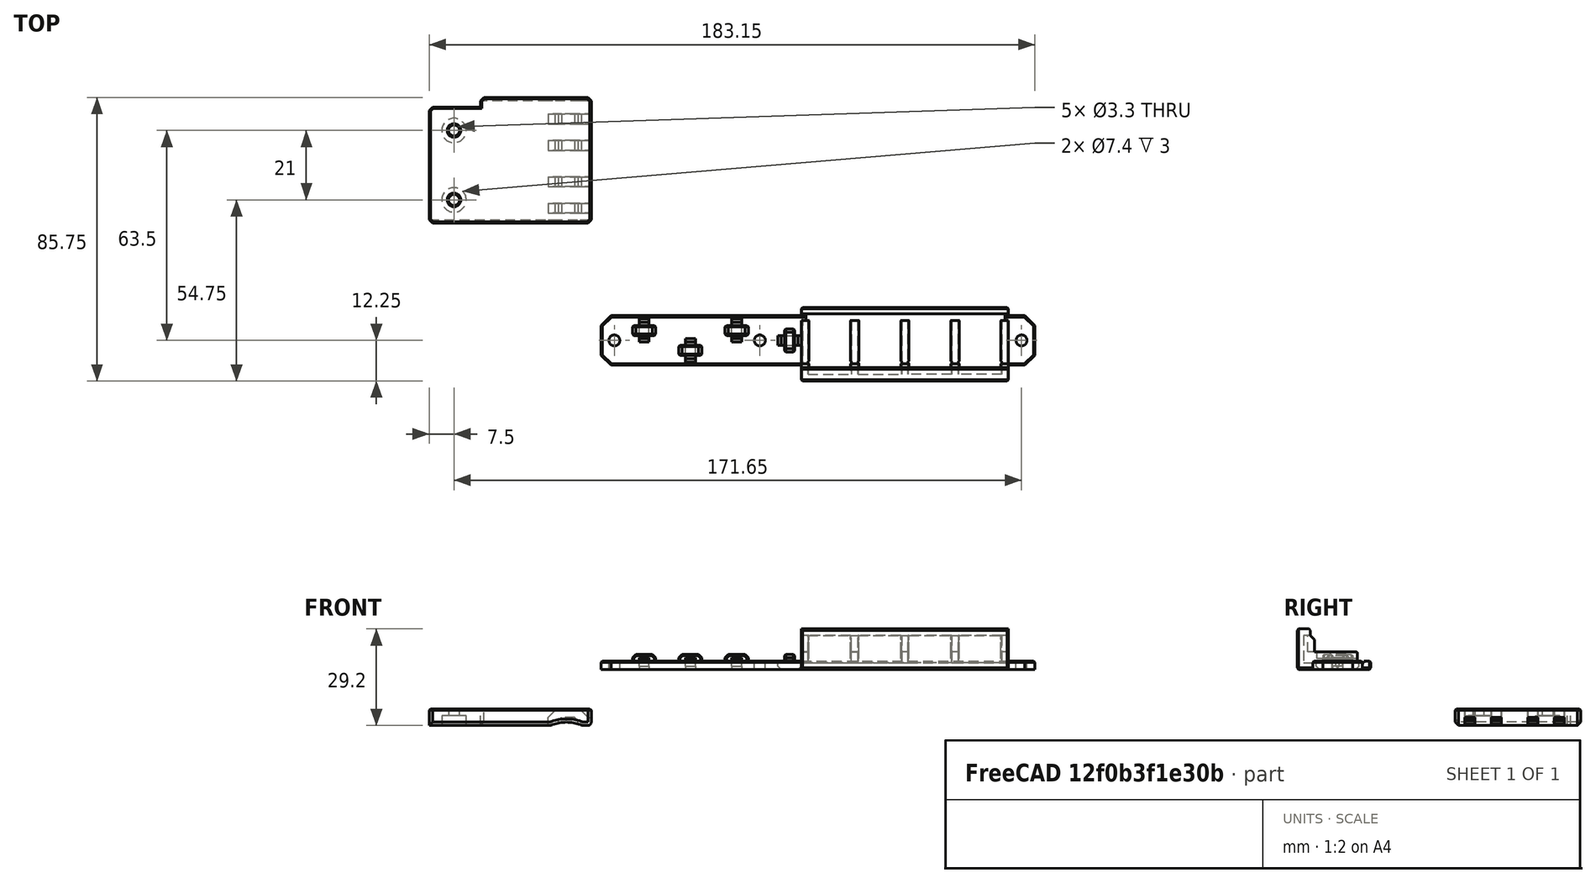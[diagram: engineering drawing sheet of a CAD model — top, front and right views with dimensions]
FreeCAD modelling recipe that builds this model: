
FCSTD DOCUMENT  (FreeCAD 0.19R24291 (Git))
Label: bed-wago-250
License: All rights reserved
LicenseURL: http://en.wikipedia.org/wiki/All_rights_reserved
objects: Part::Feature×3, Part::Box×2, Part::Cut×1, Part::MultiCommon×1, Part::MultiFuse×1
note: 8 computed .brp shape members not serialized (recipe doc carries the construction recipe); baked Part::Feature solids carry a one-line shape summary decoded from their .brp

FEATURE [Part::Feature] Part__Mirroring002  label="wago-mounter"
  Placement = pos=(0,14,4.5) rot=(0,0,1;0rad)
  shape: bbox 116 x 22.25 x 12.2 mm, 276 faces (baked)
FEATURE [Part::Feature] Fusion001001001  label="bed-cable-mounter"
  Placement = pos=(-110,77.5,-12.5) rot=(1,0,0;1.5708rad)
  shape: bbox 49 x 38 x 5 mm, 109 faces (baked)
FEATURE [Part::Box] Box  label="Cube"
  AttacherType = Attacher::AttachEngine3D
  Height = 22
  Length = 60
  Placement = pos=(19.96,-10,0) rot=(0,0,1;0rad)
  Width = 26
FEATURE [Part::Box] Box001  label="Cube001"
  AttacherType = Attacher::AttachEngine3D
  Height = 22
  Length = 60
  Placement = pos=(35.11,-10,0) rot=(0,0,1;0rad)
  Width = 26
FEATURE [Part::Feature] Part__Mirroring003  label="wago-mounter001"
  Placement = pos=(0,14,4.5) rot=(0,0,1;0rad)
  shape: bbox 116 x 22.25 x 12.2 mm, 276 faces (baked)
FEATURE [Part::Cut] Cut
  Base = -> Part__Mirroring003
  Tool = -> Box001
FEATURE [Part::MultiCommon] Common
  Placement = pos=(15.15,0,0) rot=(0,0,1;0rad)
  Shapes = -> [Box,Part__Mirroring002]
FEATURE [Part::MultiFuse] Fusion
  Refine = true
  Shapes = -> [Common,Cut]
